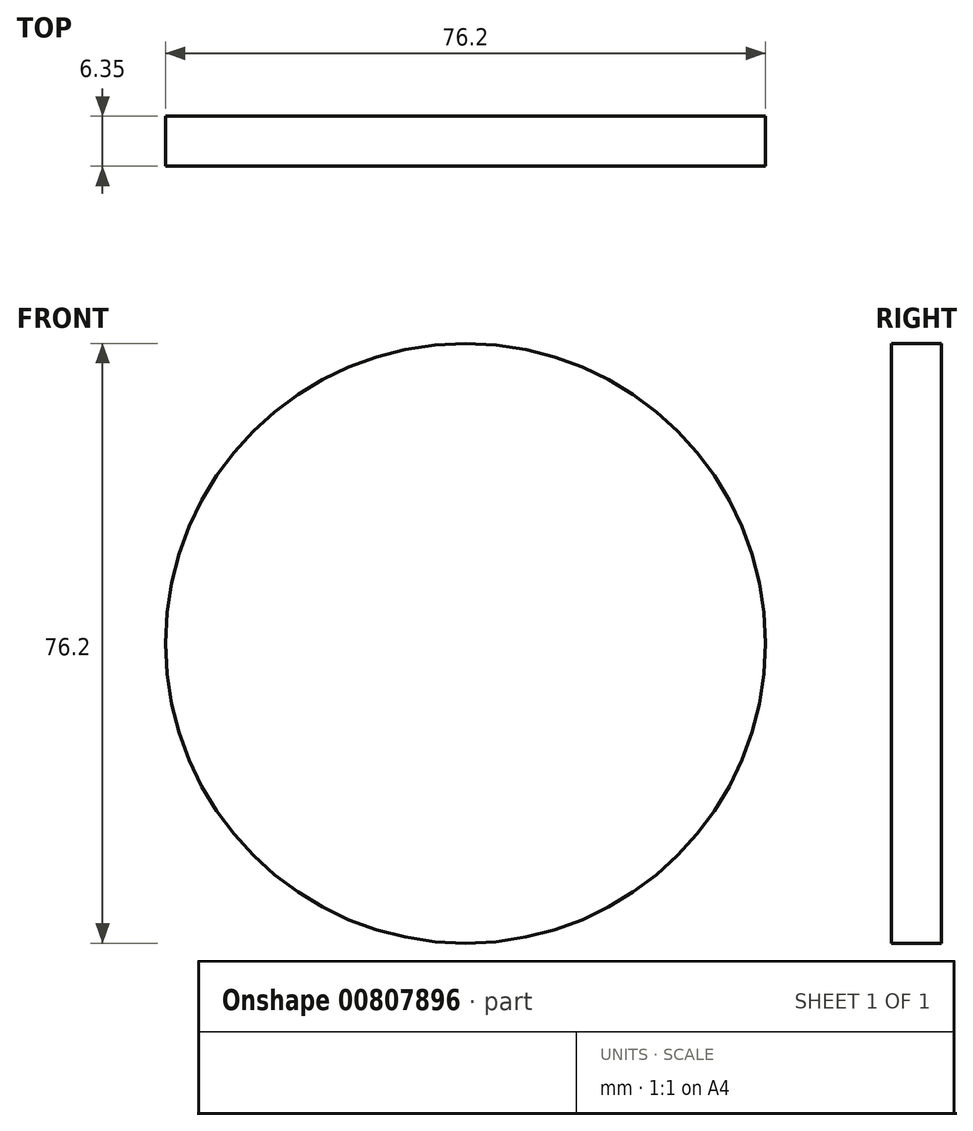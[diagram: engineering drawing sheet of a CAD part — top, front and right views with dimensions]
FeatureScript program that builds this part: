
annotation { "Feature Type Name" : "Feature", "Feature Type Description" : "" }
export const myFeature = defineFeature(function(context is Context, id is Id, definition is map)
    precondition{}
    {
        {
            var Q0;
            Q0=qCreatedBy(makeId("Front.planeOp"),FACE);
            var sketch = newSketch(context, id + "F0", { "sketchPlane" : qUnion([Q0])});
            skCircle(sketch, "E0", {"center": v(0, 0) * mm, "radius": 38.1 * mm});
            skSolve(sketch);
        }
        {
            var Q0;
            Q0=qCreatedBy(makeId("Front.planeOp"),FACE);
            var sketch = newSketch(context, id + "F1", { "sketchPlane" : qUnion([Q0])});
            skLineSegment(sketch, "E1.bottom", {"start": v(15.88, -15.87) * mm, "end": v(-15.88, -15.88) * mm});
            skLineSegment(sketch, "E1.top", {"start": v(15.88, 15.88) * mm, "end": v(-15.88, 15.87) * mm});
            skLineSegment(sketch, "E1.left", {"start": v(15.88, -15.87) * mm, "end": v(15.88, 15.88) * mm});
            skLineSegment(sketch, "E1.right", {"start": v(-15.88, -15.88) * mm, "end": v(-15.88, 15.87) * mm});
            skPoint(sketch, "E1.middle", {"position": v(0, 0) * mm});
            skSolve(sketch);
        }
        {
            var Q0;
            Q0 = qSketchRegion(id + "F0", true);
            extrude(context, id + "F2", {"entities" : qUnion([Q0]), "depth" : 6.35 * mm, "offsetDistance" : 25.4 * mm});
        }
    });
